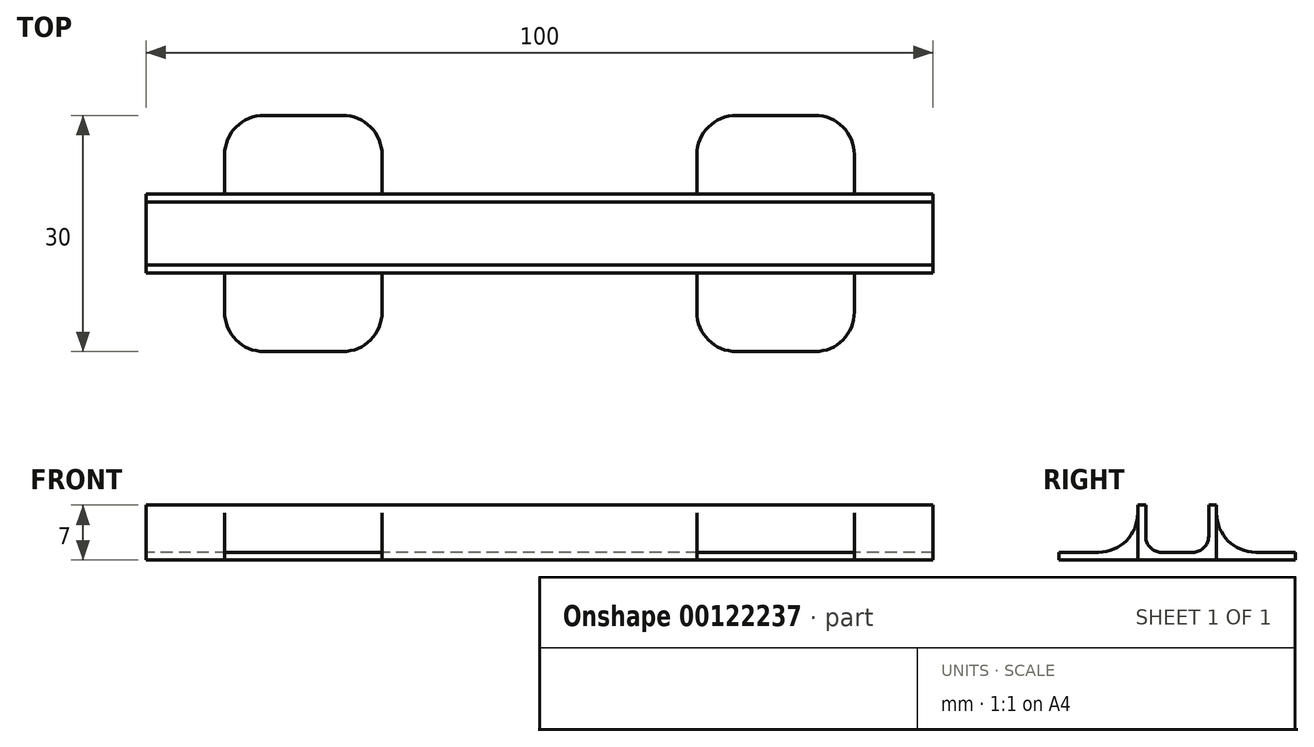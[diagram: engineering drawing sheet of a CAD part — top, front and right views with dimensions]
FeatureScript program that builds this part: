
annotation { "Feature Type Name" : "Feature", "Feature Type Description" : "" }
export const myFeature = defineFeature(function(context is Context, id is Id, definition is map)
    precondition{}
    {
        {
            var Q0;
            Q0=qCreatedBy(makeId("Right.planeOp"),FACE);
            var sketch = newSketch(context, id + "F0", { "sketchPlane" : qUnion([Q0])});
            skLineSegment(sketch, "E0", {"start": v(-5, 7) * mm, "end": v(-5, 0) * mm});
            skLineSegment(sketch, "E1", {"start": v(-5, 0) * mm, "end": v(5, 0) * mm});
            skLineSegment(sketch, "E2", {"start": v(5, 0) * mm, "end": v(5, 7) * mm});
            skLineSegment(sketch, "E3", {"start": v(5, 7) * mm, "end": v(4, 7) * mm});
            skLineSegment(sketch, "E4", {"start": v(4, 7) * mm, "end": v(4, 1) * mm});
            skLineSegment(sketch, "E5", {"start": v(4, 1) * mm, "end": v(-4, 1) * mm});
            skLineSegment(sketch, "E6", {"start": v(-4, 1) * mm, "end": v(-4, 7) * mm});
            skLineSegment(sketch, "E7", {"start": v(-4, 7) * mm, "end": v(-5, 7) * mm});
            skSolve(sketch);
        }
        {
            var Q0;
            Q0=makeQuery(id+"F0.imprint","IMPRINT",FACE,{"disambiguationData":[TD([[makeQuery(id+"F0.imprint","IMPRINT",EDGE,{"derivedFrom":sQuery(id+"F0.wireOp",EDGE,"E0")}),1.0]])]});
            extrude(context, id + "F1", {"entities" : qUnion([Q0]), "depth" : 100 * mm});
        }
        {
            var Q0;
            Q0=qCreatedBy(makeId("Top.planeOp"),FACE);
            var sketch = newSketch(context, id + "F2", { "sketchPlane" : qUnion([Q0])});
            skLineSegment(sketch, "E8.bottom", {"start": v(10, 15) * mm, "end": v(30, 15) * mm});
            skLineSegment(sketch, "E8.top", {"start": v(10, -15) * mm, "end": v(30, -15) * mm});
            skLineSegment(sketch, "E8.left", {"start": v(10, 15) * mm, "end": v(10, -15) * mm});
            skLineSegment(sketch, "E8.right", {"start": v(30, 15) * mm, "end": v(30, -15) * mm});
            skLineSegment(sketch, "E9.bottom", {"start": v(70, 15) * mm, "end": v(90, 15) * mm});
            skLineSegment(sketch, "E9.top", {"start": v(70, -15) * mm, "end": v(90, -15) * mm});
            skLineSegment(sketch, "E9.left", {"start": v(70, 15) * mm, "end": v(70, -15) * mm});
            skLineSegment(sketch, "E9.right", {"start": v(90, 15) * mm, "end": v(90, -15) * mm});
            skSolve(sketch);
        }
        {
            var Q0;
            Q0=makeQuery(id+"F2.imprint","IMPRINT",FACE,{"disambiguationData":[TD([[makeQuery(id+"F2.imprint","IMPRINT",EDGE,{"derivedFrom":sQuery(id+"F2.wireOp",EDGE,"E8.bottom")}),-1.0]])]});
            var Q1;
            Q1=makeQuery(id+"F2.imprint","IMPRINT",FACE,{"disambiguationData":[TD([[makeQuery(id+"F2.imprint","IMPRINT",EDGE,{"derivedFrom":sQuery(id+"F2.wireOp",EDGE,"E9.bottom")}),-1.0]])]});
            extrude(context, id + "F3", {"entities" : qUnion([Q0, Q1]), "operationType" : NewBodyOperationType.ADD, "depth" : 1 * mm});
        }
        {
            var Q0;
            Q0=makeQuery(id+"F3.boolean.opBoolean","INTERSECT",EDGE,{"derivedFrom":[makeQuery(id+"F1.opExtrude","SWEPT_FACE",FACE,{"disambiguationData":[OSD([sQuery(id+"F0.wireOp",EDGE,"E0")])]}),makeQuery(id+"F3.opExtrude","CAP_FACE",FACE,{"disambiguationData":[OSD([sQuery(id+"F2.wireOp",EDGE,"E8.bottom"),sQuery(id+"F2.wireOp",EDGE,"E8.top"),sQuery(id+"F2.wireOp",EDGE,"E8.left"),sQuery(id+"F2.wireOp",EDGE,"E8.right")])],"isStart":false})]});
            var Q1;
            Q1=makeQuery(id+"F3.boolean.opBoolean","INTERSECT",EDGE,{"derivedFrom":[makeQuery(id+"F1.opExtrude","SWEPT_FACE",FACE,{"disambiguationData":[OSD([sQuery(id+"F0.wireOp",EDGE,"E0")])]}),makeQuery(id+"F3.opExtrude","CAP_FACE",FACE,{"disambiguationData":[OSD([sQuery(id+"F2.wireOp",EDGE,"E9.bottom"),sQuery(id+"F2.wireOp",EDGE,"E9.top"),sQuery(id+"F2.wireOp",EDGE,"E9.left"),sQuery(id+"F2.wireOp",EDGE,"E9.right")])],"isStart":false})]});
            var Q2;
            Q2=makeQuery(id+"F3.boolean.opBoolean","INTERSECT",EDGE,{"derivedFrom":[makeQuery(id+"F1.opExtrude","SWEPT_FACE",FACE,{"disambiguationData":[OSD([sQuery(id+"F0.wireOp",EDGE,"E2")])]}),makeQuery(id+"F3.opExtrude","CAP_FACE",FACE,{"disambiguationData":[OSD([sQuery(id+"F2.wireOp",EDGE,"E8.bottom"),sQuery(id+"F2.wireOp",EDGE,"E8.top"),sQuery(id+"F2.wireOp",EDGE,"E8.left"),sQuery(id+"F2.wireOp",EDGE,"E8.right")])],"isStart":false})]});
            var Q3;
            Q3=makeQuery(id+"F3.boolean.opBoolean","INTERSECT",EDGE,{"derivedFrom":[makeQuery(id+"F1.opExtrude","SWEPT_FACE",FACE,{"disambiguationData":[OSD([sQuery(id+"F0.wireOp",EDGE,"E2")])]}),makeQuery(id+"F3.opExtrude","CAP_FACE",FACE,{"disambiguationData":[OSD([sQuery(id+"F2.wireOp",EDGE,"E9.bottom"),sQuery(id+"F2.wireOp",EDGE,"E9.top"),sQuery(id+"F2.wireOp",EDGE,"E9.left"),sQuery(id+"F2.wireOp",EDGE,"E9.right")])],"isStart":false})]});
            var Q4;
            Q4=makeQuery(id+"F3.opExtrude","SWEPT_EDGE",EDGE,{"disambiguationData":[OSD([sQuery(id+"F2.wireOp",EDGE,"E8.top"),sQuery(id+"F2.wireOp",EDGE,"E8.left")])]});
            var Q5;
            Q5=makeQuery(id+"F3.opExtrude","SWEPT_EDGE",EDGE,{"disambiguationData":[OSD([sQuery(id+"F2.wireOp",EDGE,"E8.top"),sQuery(id+"F2.wireOp",EDGE,"E8.right")])]});
            var Q6;
            Q6=makeQuery(id+"F3.opExtrude","SWEPT_EDGE",EDGE,{"disambiguationData":[OSD([sQuery(id+"F2.wireOp",EDGE,"E9.top"),sQuery(id+"F2.wireOp",EDGE,"E9.left")])]});
            var Q7;
            Q7=makeQuery(id+"F3.opExtrude","SWEPT_EDGE",EDGE,{"disambiguationData":[OSD([sQuery(id+"F2.wireOp",EDGE,"E9.top"),sQuery(id+"F2.wireOp",EDGE,"E9.right")])]});
            var Q8;
            Q8=makeQuery(id+"F3.opExtrude","SWEPT_EDGE",EDGE,{"disambiguationData":[OSD([sQuery(id+"F2.wireOp",EDGE,"E8.bottom"),sQuery(id+"F2.wireOp",EDGE,"E8.left")])]});
            var Q9;
            Q9=makeQuery(id+"F3.opExtrude","SWEPT_EDGE",EDGE,{"disambiguationData":[OSD([sQuery(id+"F2.wireOp",EDGE,"E8.bottom"),sQuery(id+"F2.wireOp",EDGE,"E8.right")])]});
            var Q10;
            Q10=makeQuery(id+"F3.opExtrude","SWEPT_EDGE",EDGE,{"disambiguationData":[OSD([sQuery(id+"F2.wireOp",EDGE,"E9.bottom"),sQuery(id+"F2.wireOp",EDGE,"E9.left")])]});
            var Q11;
            Q11=makeQuery(id+"F3.opExtrude","SWEPT_EDGE",EDGE,{"disambiguationData":[OSD([sQuery(id+"F2.wireOp",EDGE,"E9.bottom"),sQuery(id+"F2.wireOp",EDGE,"E9.right")])]});
            fillet(context, id + "F4", {"entities" : qUnion([Q0, Q1, Q2, Q3, Q4, Q5, Q6, Q7, Q8, Q9, Q10, Q11]), "radius" : 5 * mm, "tangentPropagation" : true, "allowEdgeOverflow" : false});
        }
        {
            var Q0;
            Q0=makeQuery(id+"F3.boolean.opBoolean","INTERSECT",EDGE,{"disambiguationData":[OD(0.0)],"derivedFrom":[makeQuery(id+"F3.opExtrude","CAP_FACE",FACE,{"disambiguationData":[OSD([sQuery(id+"F2.wireOp",EDGE,"E8.bottom"),sQuery(id+"F2.wireOp",EDGE,"E8.top"),sQuery(id+"F2.wireOp",EDGE,"E8.left"),sQuery(id+"F2.wireOp",EDGE,"E8.right")])],"isStart":false}),makeQuery(id+"F3.opExtrude","CAP_FACE",FACE,{"disambiguationData":[OSD([sQuery(id+"F2.wireOp",EDGE,"E9.bottom"),sQuery(id+"F2.wireOp",EDGE,"E9.top"),sQuery(id+"F2.wireOp",EDGE,"E9.left"),sQuery(id+"F2.wireOp",EDGE,"E9.right")])],"isStart":false})]});
            var Q1;
            Q1=makeQuery(id+"F3.boolean.opBoolean","INTERSECT",EDGE,{"disambiguationData":[OD(1.0)],"derivedFrom":[makeQuery(id+"F3.opExtrude","CAP_FACE",FACE,{"disambiguationData":[OSD([sQuery(id+"F2.wireOp",EDGE,"E8.bottom"),sQuery(id+"F2.wireOp",EDGE,"E8.top"),sQuery(id+"F2.wireOp",EDGE,"E8.left"),sQuery(id+"F2.wireOp",EDGE,"E8.right")])],"isStart":false}),makeQuery(id+"F3.opExtrude","CAP_FACE",FACE,{"disambiguationData":[OSD([sQuery(id+"F2.wireOp",EDGE,"E9.bottom"),sQuery(id+"F2.wireOp",EDGE,"E9.top"),sQuery(id+"F2.wireOp",EDGE,"E9.left"),sQuery(id+"F2.wireOp",EDGE,"E9.right")])],"isStart":false})]});
            fillet(context, id + "F5", {"entities" : qUnion([Q0, Q1]), "radius" : 2 * mm, "tangentPropagation" : true, "allowEdgeOverflow" : false});
        }
    });
